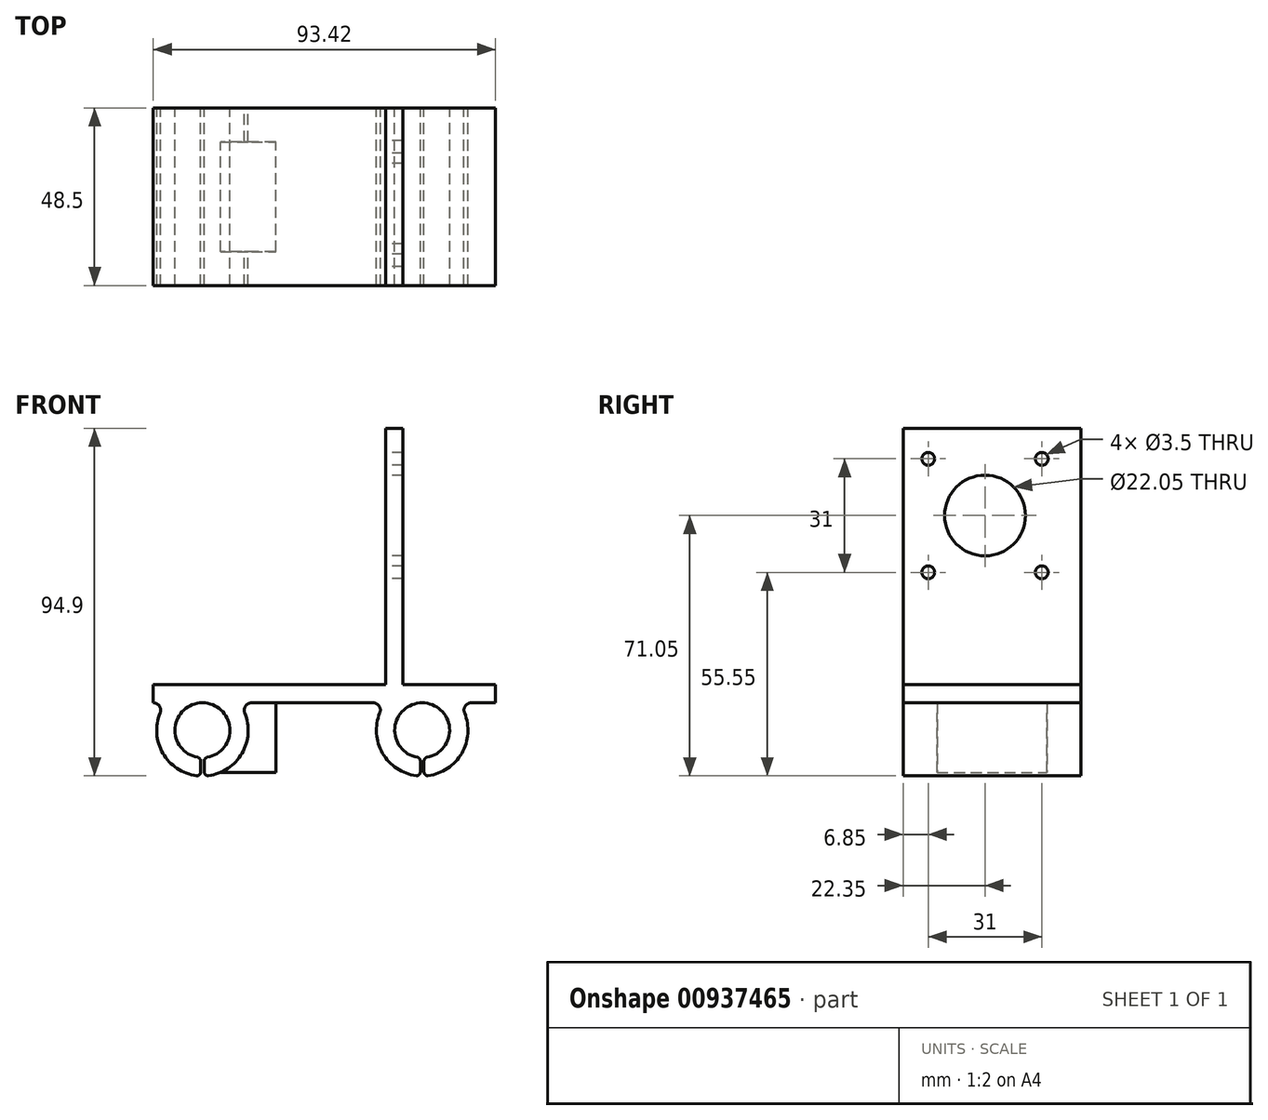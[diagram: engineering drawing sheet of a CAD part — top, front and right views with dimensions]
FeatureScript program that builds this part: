
annotation { "Feature Type Name" : "Feature", "Feature Type Description" : "" }
export const myFeature = defineFeature(function(context is Context, id is Id, definition is map)
    precondition{}
    {
        {
            var Q0;
            Q0=qCreatedBy(makeId("Front.planeOp"),FACE);
            var sketch = newSketch(context, id + "F0", { "sketchPlane" : qUnion([Q0])});
            skCircle(sketch, "E0", {"center": v(-30, 0) * mm, "radius": 4 * mm});
            skCircle(sketch, "E1", {"center": v(30, 0) * mm, "radius": 4 * mm});
            skSolve(sketch);
        }
        {
            var Q0;
            Q0=qCreatedBy(makeId("Front.planeOp"),FACE);
            var sketch = newSketch(context, id + "F1", { "sketchPlane" : qUnion([Q0])});
            skArc(sketch, "E2", {"start": v(-28.68, -7.38) * mm, "mid": v(-30, 7.5) * mm, "end": v(-31.32, -7.38) * mm});
            skArc(sketch, "E3", {"start": v(31.32, -7.38) * mm, "mid": v(30, 7.5) * mm, "end": v(28.68, -7.38) * mm});
            skArc(sketch, "E4", {"start": v(-41.57, 4.74) * mm, "mid": v(-40.81, -6.27) * mm, "end": v(-31.63, -12.4) * mm});
            skArc(sketch, "E5", {"start": v(18.43, 4.74) * mm, "mid": v(19.19, -6.27) * mm, "end": v(28.37, -12.4) * mm});
            skLineSegment(sketch, "E6.right", {"start": v(50, 12.5) * mm, "end": v(50, 7.5) * mm});
            skLineSegment(sketch, "E7.trimOffspring", {"start": v(-16.58, 7.5) * mm, "end": v(16.58, 7.5) * mm});
            skLineSegment(sketch, "E8.trimOffspring", {"start": v(43.42, 7.5) * mm, "end": v(50, 7.5) * mm});
            skLineSegment(sketch, "E9.left", {"start": v(-30.5, -8.37) * mm, "end": v(-30.5, -11.4) * mm});
            skLineSegment(sketch, "E9.right", {"start": v(-29.5, -8.37) * mm, "end": v(-29.5, -11.4) * mm});
            skLineSegment(sketch, "E10.left", {"start": v(29.5, -8.37) * mm, "end": v(29.5, -11.4) * mm});
            skLineSegment(sketch, "E10.right", {"start": v(30.5, -8.37) * mm, "end": v(30.5, -11.4) * mm});
            skArc(sketch, "E11.trimOffspring", {"start": v(-28.37, -12.4) * mm, "mid": v(-19.19, -6.27) * mm, "end": v(-18.43, 4.74) * mm});
            skArc(sketch, "E12.trimOffspring", {"start": v(31.63, -12.4) * mm, "mid": v(40.81, -6.27) * mm, "end": v(41.57, 4.74) * mm});
            skPoint(sketch, "E13.visualSharp", {"position": v(-30.5, -7.48) * mm});
            skArc(sketch, "E13.filletArc", {"start": v(-30.5, -8.37) * mm, "mid": v(-30.73, -7.72) * mm, "end": v(-31.32, -7.38) * mm});
            skPoint(sketch, "E14.visualSharp", {"position": v(-29.5, -7.48) * mm});
            skArc(sketch, "E14.filletArc", {"start": v(-28.68, -7.38) * mm, "mid": v(-29.27, -7.72) * mm, "end": v(-29.5, -8.37) * mm});
            skPoint(sketch, "E15.visualSharp", {"position": v(29.5, -7.48) * mm});
            skArc(sketch, "E15.filletArc", {"start": v(29.5, -8.37) * mm, "mid": v(29.27, -7.72) * mm, "end": v(28.68, -7.38) * mm});
            skPoint(sketch, "E16.visualSharp", {"position": v(30.5, -7.48) * mm});
            skArc(sketch, "E16.filletArc", {"start": v(31.32, -7.38) * mm, "mid": v(30.73, -7.72) * mm, "end": v(30.5, -8.37) * mm});
            skPoint(sketch, "E17.visualSharp", {"position": v(30.5, -12.49) * mm});
            skArc(sketch, "E17.filletArc", {"start": v(30.5, -11.4) * mm, "mid": v(30.84, -12.15) * mm, "end": v(31.63, -12.4) * mm});
            skPoint(sketch, "E18.visualSharp", {"position": v(29.5, -12.49) * mm});
            skArc(sketch, "E18.filletArc", {"start": v(28.37, -12.4) * mm, "mid": v(29.16, -12.15) * mm, "end": v(29.5, -11.4) * mm});
            skPoint(sketch, "E19.visualSharp", {"position": v(-29.5, -12.49) * mm});
            skArc(sketch, "E19.filletArc", {"start": v(-29.5, -11.4) * mm, "mid": v(-29.16, -12.15) * mm, "end": v(-28.37, -12.4) * mm});
            skPoint(sketch, "E20.visualSharp", {"position": v(-30.5, -12.49) * mm});
            skArc(sketch, "E20.filletArc", {"start": v(-31.63, -12.4) * mm, "mid": v(-30.84, -12.15) * mm, "end": v(-30.5, -11.4) * mm});
            skPoint(sketch, "E21.visualSharp", {"position": v(-20, 7.5) * mm});
            skArc(sketch, "E21.filletArc", {"start": v(-16.58, 7.5) * mm, "mid": v(-18.24, 6.61) * mm, "end": v(-18.43, 4.74) * mm});
            skPoint(sketch, "E22.visualSharp", {"position": v(20, 7.5) * mm});
            skArc(sketch, "E22.filletArc", {"start": v(18.43, 4.74) * mm, "mid": v(18.24, 6.61) * mm, "end": v(16.58, 7.5) * mm});
            skPoint(sketch, "E23.visualSharp", {"position": v(40, 7.5) * mm});
            skArc(sketch, "E23.filletArc", {"start": v(43.42, 7.5) * mm, "mid": v(41.76, 6.61) * mm, "end": v(41.57, 4.74) * mm});
            skPoint(sketch, "E24.visualSharp", {"position": v(-40, 7.5) * mm});
            skArc(sketch, "E24.filletArc", {"start": v(-41.57, 4.74) * mm, "mid": v(-41.76, 6.61) * mm, "end": v(-43.42, 7.5) * mm});
            skLineSegment(sketch, "E25", {"start": v(0, -23.9) * mm, "end": v(0, 82.5) * mm, "construction": true});
            skLineSegment(sketch, "E26.top", {"start": v(20, 82.5) * mm, "end": v(24.75, 82.5) * mm});
            skLineSegment(sketch, "E26.left", {"start": v(20, 12.5) * mm, "end": v(20, 82.5) * mm});
            skLineSegment(sketch, "E26.right", {"start": v(24.75, 12.5) * mm, "end": v(24.75, 82.5) * mm});
            skLineSegment(sketch, "E27.trimOffspring", {"start": v(24.75, 12.5) * mm, "end": v(50, 12.5) * mm});
            skPoint(sketch, "E28", {"position": v(22.38, 82.5) * mm});
            skLineSegment(sketch, "E29", {"start": v(20, 12.5) * mm, "end": v(-43.42, 12.5) * mm});
            skLineSegment(sketch, "E30", {"start": v(-43.42, 12.5) * mm, "end": v(-43.42, 7.5) * mm});
            skSolve(sketch);
        }
        {
            var Q0;
            Q0 = qSketchRegion(id + "F1", true);
            extrude(context, id + "F2", {"entities" : qUnion([Q0]), "depth" : 24.25 * mm, "offsetDistance" : 25 * mm, "hasSecondDirection" : true, "secondDirectionOppositeDirection" : true, "secondDirectionDepth" : 24.25 * mm});
        }
        {
            var Q0;
            Q0=makeQuery(id+"F2.opExtrude","SWEPT_FACE",FACE,{"disambiguationData":[OSD([sQuery(id+"F1.wireOp",EDGE,"E26.left")])]});
            var sketch = newSketch(context, id + "F3", { "sketchPlane" : qUnion([Q0])});
            skCircle(sketch, "E31", {"center": v(1.9, 58.65) * mm, "radius": 11.03 * mm});
            skCircle(sketch, "E32", {"center": v(-13.6, 43.15) * mm, "radius": 1.75 * mm});
            skCircle(sketch, "E33.1.0", {"center": v(17.4, 43.15) * mm, "radius": 1.75 * mm});
            skCircle(sketch, "E33.2.0", {"center": v(17.4, 74.15) * mm, "radius": 1.75 * mm});
            skCircle(sketch, "E33.3.0", {"center": v(-13.6, 74.15) * mm, "radius": 1.75 * mm});
            skSolve(sketch);
        }
        {
            var Q0;
            Q0 = qSketchRegion(id + "F3", true);
            extrude(context, id + "F4", {"entities" : qUnion([Q0]), "operationType" : NewBodyOperationType.REMOVE, "endBound" : BoundingType.UP_TO_NEXT, "oppositeDirection" : true, "depth" : 25 * mm, "offsetDistance" : 25 * mm});
        }
        {
            var Q0;
            Q0=qCreatedBy(makeId("Front.planeOp"),FACE);
            var sketch = newSketch(context, id + "F5", { "sketchPlane" : qUnion([Q0])});
            skLineSegment(sketch, "E34", {"start": v(-10, 9.5) * mm, "end": v(-10, -11.5) * mm});
            skLineSegment(sketch, "E35", {"start": v(-10, -11.5) * mm, "end": v(-27.35, -11.5) * mm});
            skLineSegment(sketch, "E36", {"start": v(-27.35, -11.5) * mm, "end": v(-19.7, 0) * mm});
            skLineSegment(sketch, "E37", {"start": v(-19.7, 0) * mm, "end": v(-19.7, 9.5) * mm});
            skLineSegment(sketch, "E38", {"start": v(-19.7, 9.5) * mm, "end": v(-10, 9.5) * mm});
            skSolve(sketch);
        }
        {
            var Q0;
            Q0 = qSketchRegion(id + "F5", true);
            extrude(context, id + "F6", {"entities" : qUnion([Q0]), "operationType" : NewBodyOperationType.ADD, "depth" : 15 * mm, "offsetDistance" : 25 * mm, "hasSecondDirection" : true, "secondDirectionOppositeDirection" : true, "secondDirectionDepth" : 15 * mm});
        }
        {
            var Q0;
            Q0=makeQuery(id+"F2.opExtrude","SWEPT_EDGE",EDGE,{"disambiguationData":[OSD([sQuery(id+"F1.wireOp",EDGE,"E26.right"),sQuery(id+"F1.wireOp",EDGE,"E27.trimOffspring")])]});
            cPlane(context, id + "F7", {"entities" : qUnion([Q0]), "cplaneType" : CPlaneType.LINE_ANGLE, "offset" : 25 * mm, "angle" : 45 * degree, "width" : 150 * mm, "height" : 150 * mm});
        }
    });
